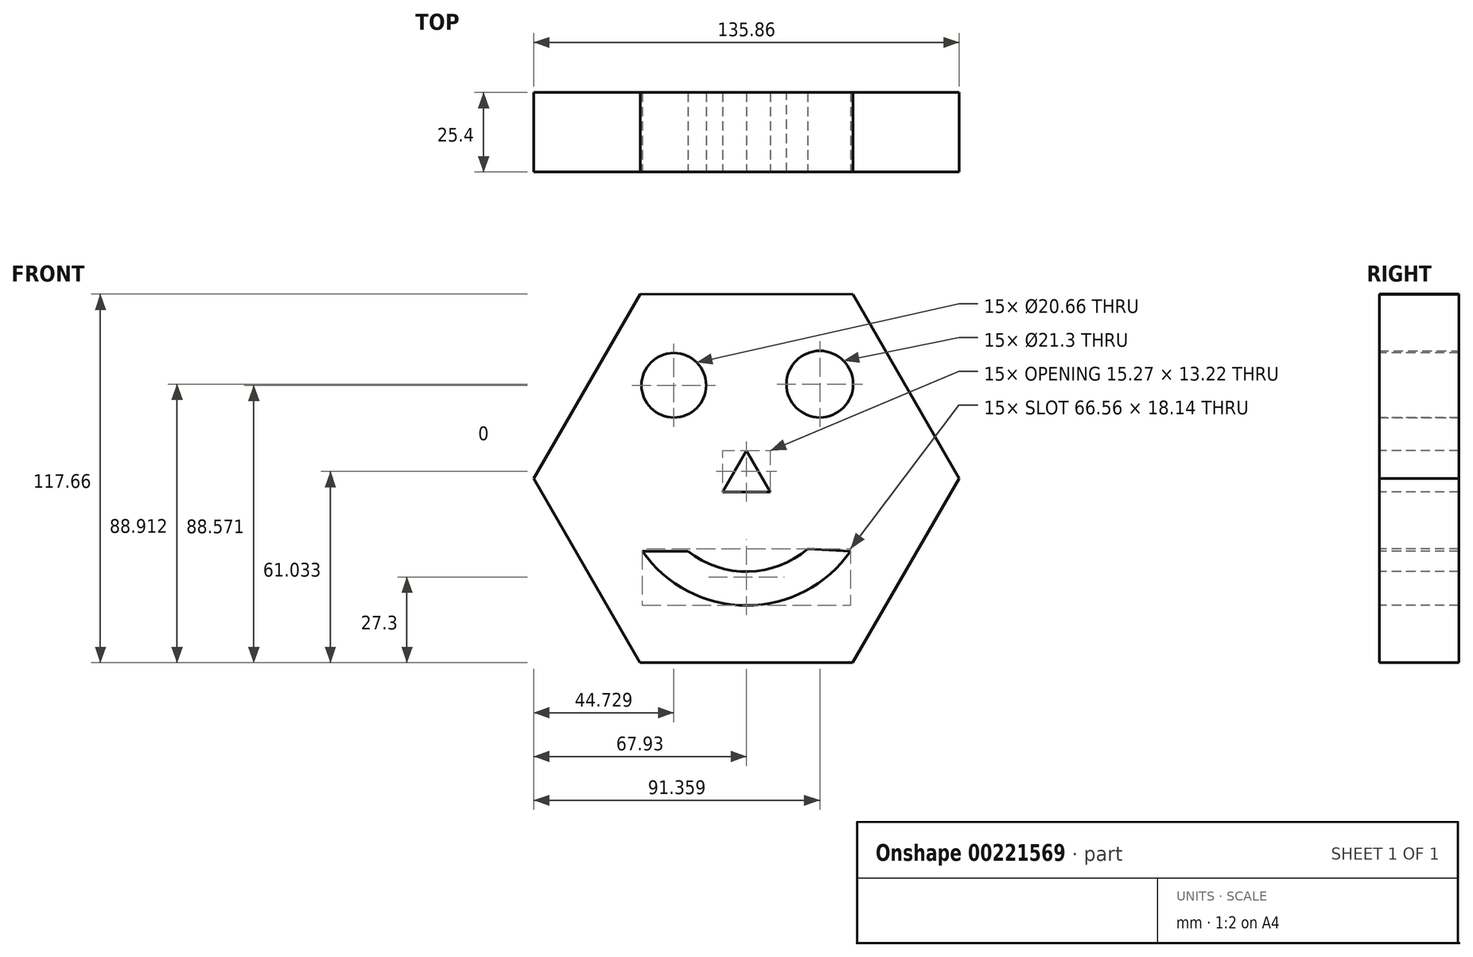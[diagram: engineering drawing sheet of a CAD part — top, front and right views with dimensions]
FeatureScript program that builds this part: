
annotation { "Feature Type Name" : "Feature", "Feature Type Description" : "" }
export const myFeature = defineFeature(function(context is Context, id is Id, definition is map)
    precondition{}
    {
        {
            var Q0;
            Q0=qCreatedBy(makeId("Front.planeOp"),FACE);
            var sketch = newSketch(context, id + "F0", { "sketchPlane" : qUnion([Q0])});
            skCircle(sketch, "E0.cCircle", {"center": v(0, 0) * mm, "radius": 58.83 * mm, "construction": true});
            skLineSegment(sketch, "E0.0", {"start": v(-33.98, -58.82) * mm, "end": v(-67.93, 0.02) * mm});
            skLineSegment(sketch, "E0.1", {"start": v(-67.93, 0.02) * mm, "end": v(-33.95, 58.83) * mm});
            skLineSegment(sketch, "E0.2", {"start": v(-33.95, 58.83) * mm, "end": v(33.98, 58.82) * mm});
            skLineSegment(sketch, "E0.3", {"start": v(33.98, 58.82) * mm, "end": v(67.93, -0.02) * mm});
            skLineSegment(sketch, "E0.4", {"start": v(67.93, -0.02) * mm, "end": v(33.95, -58.83) * mm});
            skLineSegment(sketch, "E0.5", {"start": v(33.95, -58.83) * mm, "end": v(-33.98, -58.82) * mm});
            skPoint(sketch, "E0.0.midPoint", {"position": v(-50.95, -29.4) * mm});
            skSolve(sketch);
        }
        {
            var Q0;
            Q0=makeQuery(id+"F0.imprint","IMPRINT",FACE,{"disambiguationData":[TD([[makeQuery(id+"F0.imprint","IMPRINT",EDGE,{"derivedFrom":sQuery(id+"F0.wireOp",EDGE,"E0.0")}),-1.0]])]});
            extrude(context, id + "F1", {"entities" : qUnion([Q0]), "depth" : 25.4 * mm});
        }
        {
            var Q0;
            Q0=makeQuery(id+"F1.opExtrude","CAP_FACE",FACE,{"disambiguationData":[OSD([sQuery(id+"F0.wireOp",EDGE,"E0.0"),sQuery(id+"F0.wireOp",EDGE,"E0.1"),sQuery(id+"F0.wireOp",EDGE,"E0.2"),sQuery(id+"F0.wireOp",EDGE,"E0.3"),sQuery(id+"F0.wireOp",EDGE,"E0.4"),sQuery(id+"F0.wireOp",EDGE,"E0.5")])],"isStart":false});
            var sketch = newSketch(context, id + "F2", { "sketchPlane" : qUnion([Q0])});
            skCircle(sketch, "E1", {"center": v(-23.2, 29.74) * mm, "radius": 10.33 * mm});
            skSolve(sketch);
        }
        {
            var Q0;
            Q0=makeQuery(id+"F2.imprint","IMPRINT",FACE,{"disambiguationData":[TD([[makeQuery(id+"F2.imprint","IMPRINT",EDGE,{"derivedFrom":sQuery(id+"F2.wireOp",EDGE,"E1")}),1.0]])]});
            extrude(context, id + "F3", {"entities" : qUnion([Q0]), "operationType" : NewBodyOperationType.REMOVE, "endBound" : BoundingType.THROUGH_ALL, "oppositeDirection" : true, "depth" : 25.4 * mm});
        }
        {
            var Q0;
            Q0=qCreatedBy(makeId("Front.planeOp"),FACE);
            var sketch = newSketch(context, id + "F4", { "sketchPlane" : qUnion([Q0])});
            skCircle(sketch, "E2", {"center": v(23.43, 30.08) * mm, "radius": 10.65 * mm});
            skSolve(sketch);
        }
        {
            var Q0;
            Q0 = qSketchRegion(id + "F4", true);
            extrude(context, id + "F5", {"entities" : qUnion([Q0]), "operationType" : NewBodyOperationType.REMOVE, "depth" : 25.4 * mm});
        }
        {
            var Q0;
            Q0=makeQuery(id+"F1.opExtrude","CAP_FACE",FACE,{"disambiguationData":[OSD([sQuery(id+"F0.wireOp",EDGE,"E0.0"),sQuery(id+"F0.wireOp",EDGE,"E0.1"),sQuery(id+"F0.wireOp",EDGE,"E0.2"),sQuery(id+"F0.wireOp",EDGE,"E0.3"),sQuery(id+"F0.wireOp",EDGE,"E0.4"),sQuery(id+"F0.wireOp",EDGE,"E0.5")])],"isStart":false});
            var sketch = newSketch(context, id + "F6", { "sketchPlane" : qUnion([Q0])});
            skCircle(sketch, "E3.cCircle", {"center": v(0, 0) * mm, "radius": 4.4 * mm, "construction": true});
            skLineSegment(sketch, "E3.0", {"start": v(0, 8.81) * mm, "end": v(7.63, -4.4) * mm});
            skLineSegment(sketch, "E3.1", {"start": v(7.63, -4.4) * mm, "end": v(-7.63, -4.4) * mm});
            skLineSegment(sketch, "E3.2", {"start": v(-7.63, -4.4) * mm, "end": v(0, 8.81) * mm});
            skSolve(sketch);
        }
        {
            var Q0;
            Q0=makeQuery(id+"F6.imprint","IMPRINT",FACE,{"disambiguationData":[TD([[makeQuery(id+"F6.imprint","IMPRINT",EDGE,{"derivedFrom":sQuery(id+"F6.wireOp",EDGE,"E3.0")}),-1.0]])]});
            extrude(context, id + "F7", {"entities" : qUnion([Q0]), "operationType" : NewBodyOperationType.REMOVE, "oppositeDirection" : true, "depth" : 25.4 * mm});
        }
        {
            var Q0;
            Q0=makeQuery(id+"F1.opExtrude","CAP_FACE",FACE,{"disambiguationData":[OSD([sQuery(id+"F0.wireOp",EDGE,"E0.0"),sQuery(id+"F0.wireOp",EDGE,"E0.1"),sQuery(id+"F0.wireOp",EDGE,"E0.2"),sQuery(id+"F0.wireOp",EDGE,"E0.3"),sQuery(id+"F0.wireOp",EDGE,"E0.4"),sQuery(id+"F0.wireOp",EDGE,"E0.5")])],"isStart":false});
            var sketch = newSketch(context, id + "F8", { "sketchPlane" : qUnion([Q0])});
            skArc(sketch, "E4", {"start": v(-33.28, -23.25) * mm, "mid": v(0, -40.6) * mm, "end": v(33.28, -23.25) * mm});
            skArc(sketch, "E5", {"start": v(-18.62, -23.25) * mm, "mid": v(0.62, -29.78) * mm, "end": v(19.56, -22.46) * mm});
            skLineSegment(sketch, "E6", {"start": v(-33.28, -23.25) * mm, "end": v(-18.62, -23.25) * mm});
            skLineSegment(sketch, "E7", {"start": v(19.56, -22.46) * mm, "end": v(33.28, -23.25) * mm});
            skSolve(sketch);
        }
        {
            var Q0;
            Q0=makeQuery(id+"F8.imprint","IMPRINT",FACE,{"disambiguationData":[TD([[makeQuery(id+"F8.imprint","IMPRINT",EDGE,{"derivedFrom":sQuery(id+"F8.wireOp",EDGE,"E4")}),1.0]])]});
            extrude(context, id + "F9", {"entities" : qUnion([Q0]), "operationType" : NewBodyOperationType.REMOVE, "oppositeDirection" : true, "depth" : 25.4 * mm});
        }
    });
